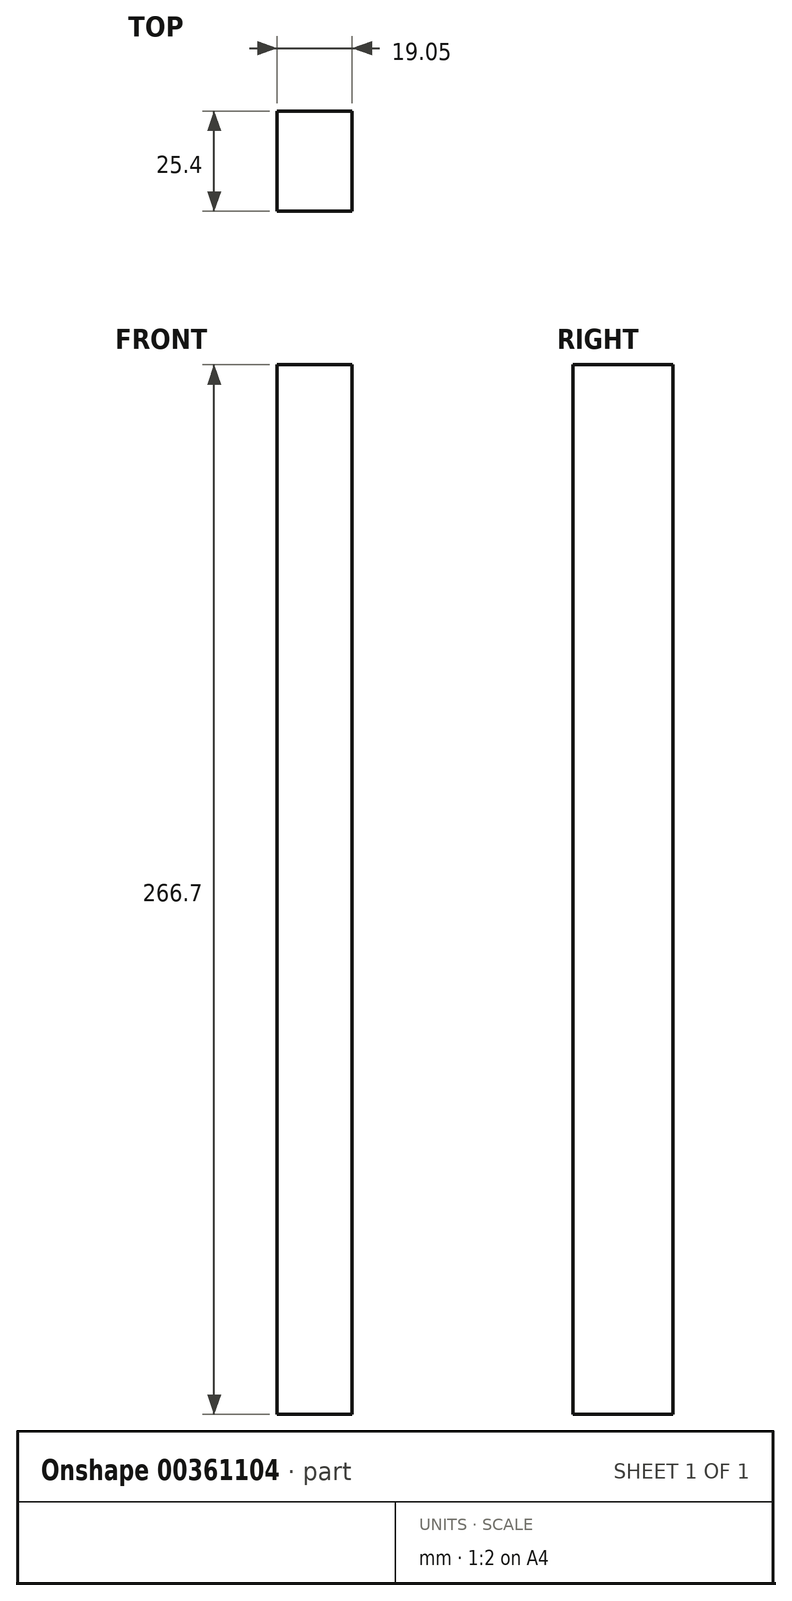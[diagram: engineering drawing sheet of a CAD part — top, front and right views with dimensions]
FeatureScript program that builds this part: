
annotation { "Feature Type Name" : "Feature", "Feature Type Description" : "" }
export const myFeature = defineFeature(function(context is Context, id is Id, definition is map)
    precondition{}
    {
        {
            var Q0;
            Q0=qCreatedBy(makeId("Right.planeOp"),FACE);
            var sketch = newSketch(context, id + "F0", { "sketchPlane" : qUnion([Q0])});
            skLineSegment(sketch, "E0.bottom", {"start": v(-115.08, 121.38) * mm, "end": v(-89.68, 121.38) * mm});
            skLineSegment(sketch, "E0.top", {"start": v(-115.08, -145.32) * mm, "end": v(-89.68, -145.32) * mm});
            skLineSegment(sketch, "E0.left", {"start": v(-115.08, 121.38) * mm, "end": v(-115.08, -145.32) * mm});
            skLineSegment(sketch, "E0.right", {"start": v(-89.68, 121.38) * mm, "end": v(-89.68, -145.32) * mm});
            skSolve(sketch);
        }
        {
            var Q0;
            Q0=qSketchRegion(id+"F0",true);
            extrude(context, id + "F1", {"entities" : qUnion([Q0]), "depth" : 19.05 * mm});
        }
    });
